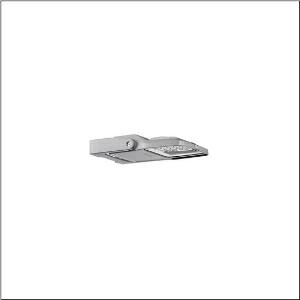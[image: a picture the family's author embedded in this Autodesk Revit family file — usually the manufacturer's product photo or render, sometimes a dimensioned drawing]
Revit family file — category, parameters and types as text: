
# Revit family: floodlight_fl_21_iq_micro___pl52_5xa7762a4d2a_e4f8
name_source: partatom
category: Lighting Fixtures
units: mm (PartAtom-declared; Revit-internal decimal feet)

## family parameters
Cut with Voids When Loaded = No
Host = Face
Light Source = No
Part Type = Normal
Room Calculation Point = No
Round Connector Dimension = Use Diameter
Shared = No

## types (1)
- --- (1 x LED, 3010 lm, 23.1 W, 4000K)
    Apparent Load = 23 VA
    CIE Flux Codes = 26 60 98 100 100
    Color Rendering = 70
    Color Temperature = 4000K
    Default Elevation = 1800 mm
    Description = Floodlight FL 21 iQ micro, floodlight, primary light control with lens, of PMMA, primary optical cover: protective disc, of toughened safety glass, transparent, light distribution: PL52, light emission: direct distribution, installation type: surface-mounted, LED, High Power LED, rated luminous flux: 3.010lm, luminous efficacy: 130lm/W, light colour: 740, colour temperature: 4000K, control: Auto-Match, Temp-Guard, Night-Set, Smart-Wire, Desk-Remote (wireless, voltage-free reading and setting of iQ features in the workshop via application-optimized NFC function/RFID function), optimised constant luminous flux control (CLO 2.0), Street-Remote, with terminal, 6-pole, mains connection: 220..240V, AC, 50/60Hz, start of lifetime: 23W, end of service life: 24W, reduction: 11W, luminaire housing, of diecast aluminium, powder-coated, Siteco® metallic grey (DB 702S), corrosivity category C5 mid according to DIN EN ISO 12944, sealing non-destructively replaceable, design bracket, of diecast aluminium, powder-coated, Siteco® metallic grey (DB 702S), protection rating (complete): IP66, insulation class (complete): insulation class II (safety insulation), certification: CE, ENEC, VDE, protection symbol: D, impact resistance: IK07, permissible operating ambient temperature: -40..+40°C, permissible operating ambient temperature for outdoor applications: -40..+50°C, standard: DIN EN 12944, LABS conformity tested according to VDMA 24364:2018-05, packaging unit: 1 piece

Light Distribution: PL52
    Height = 65 mm
    Lamp = 1 x LED
    Lamp Light Flux = 3010 lm
    Lamp Power = 23.1 W
    Lamp count = 1
    Length = 312 mm
    Luminous efficacy = 130 lm/W
    Manufacturer = Siteco
    ModVariant = No
    Model = 5XA7762A4D2A
    Mounting Place = Wall
    Mounting Type = Surface mounted
    Number of Poles = 1
    OnlyDefault = Yes
    Power Factor = 1
    Product Name = Floodlight FL 21 iQ micro | PL52
    Product group = floodlight | wall mounted
    ProductGroupID = 2001
    Protection Class = Protection class II
    Protection Degree = IP 66
    RLX_Detail_Level = 1
    RLX_Emergency_Light_Flux = 0 lm
    RLX_Emergency_Type = 0
    RLX_Emergency_Type_DB = No
    RlxData = <blob elided: 97405 chars, md5=157fc312>
    Socket = socket
    Standby Power = 0 W
    System Light Flux = 3010 lm
    System Power = 23 W
    Type Comments = factory setting: luminous flux: 100 % | dim-lin: 254 | 455 mA
    Type Image = l_1006878.jpg
    URL = http://relux.com
    VarID = @adj_149059
    Voltage = 0 V
    Weight = 0.00 kg
    Width = 230 mm

## geometry (parser evidence)
native form markers: Blend x4, Sweep x12
no freeform markers — native parametric forms only
